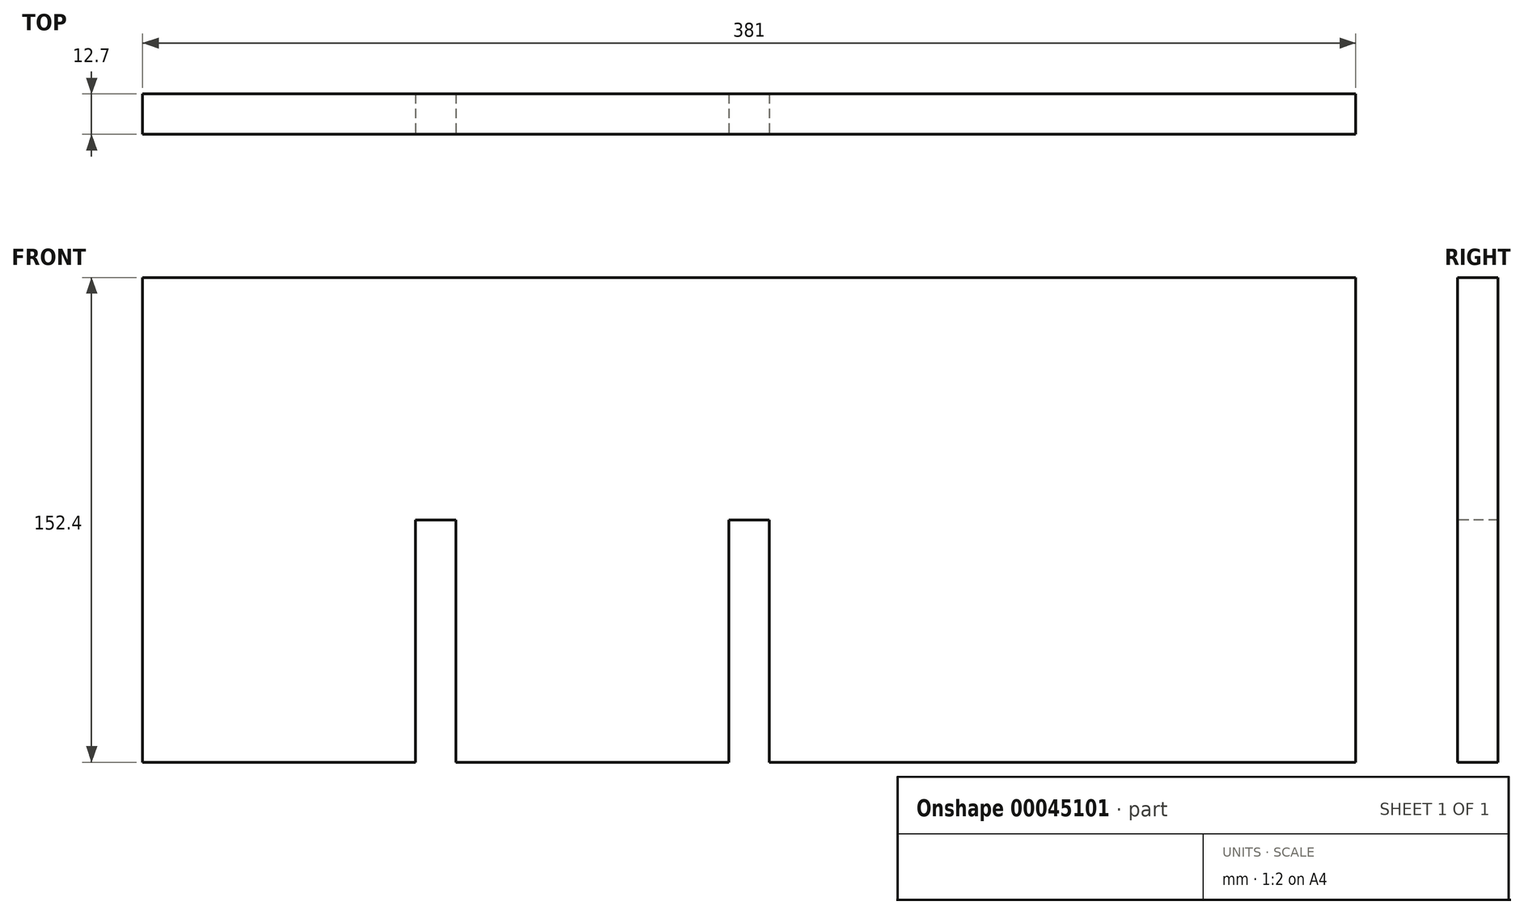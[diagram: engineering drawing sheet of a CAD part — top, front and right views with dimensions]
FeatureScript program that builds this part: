
annotation { "Feature Type Name" : "Feature", "Feature Type Description" : "" }
export const myFeature = defineFeature(function(context is Context, id is Id, definition is map)
    precondition{}
    {
        {
            var Q0;
            Q0=qCreatedBy(makeId("Front.planeOp"),FACE);
            var sketch = newSketch(context, id + "F0", { "sketchPlane" : qUnion([Q0])});
            skLineSegment(sketch, "E0.bottom", {"start": v(-134.6, 99.97) * mm, "end": v(246.4, 99.97) * mm});
            skLineSegment(sketch, "E0.top", {"start": v(-134.6, -52.43) * mm, "end": v(246.4, -52.43) * mm});
            skLineSegment(sketch, "E0.left", {"start": v(-134.6, 99.97) * mm, "end": v(-134.6, -52.43) * mm});
            skLineSegment(sketch, "E0.right", {"start": v(246.4, 99.97) * mm, "end": v(246.4, -52.43) * mm});
            skSolve(sketch);
        }
        {
            var Q0;
            Q0=makeQuery(id+"F0.imprint","IMPRINT",FACE,{"disambiguationData":[TD([[makeQuery(id+"F0.imprint","IMPRINT",EDGE,{"derivedFrom":sQuery(id+"F0.wireOp",EDGE,"E0.bottom")}),-1.0]])]});
            extrude(context, id + "F1", {"entities" : qUnion([Q0]), "depth" : 12.7 * mm});
        }
        {
            var Q0;
            Q0=makeQuery(id+"F1.opExtrude","CAP_FACE",FACE,{"disambiguationData":[OSD([sQuery(id+"F0.wireOp",EDGE,"E0.bottom"),sQuery(id+"F0.wireOp",EDGE,"E0.top"),sQuery(id+"F0.wireOp",EDGE,"E0.left"),sQuery(id+"F0.wireOp",EDGE,"E0.right")])],"isStart":false});
            var sketch = newSketch(context, id + "F2", { "sketchPlane" : qUnion([Q0])});
            skLineSegment(sketch, "E1.bottom", {"start": v(-48.87, -52.43) * mm, "end": v(-36.17, -52.43) * mm});
            skLineSegment(sketch, "E1.top", {"start": v(-48.87, 23.77) * mm, "end": v(-36.17, 23.77) * mm});
            skLineSegment(sketch, "E1.left", {"start": v(-48.87, -52.43) * mm, "end": v(-48.87, 23.77) * mm});
            skLineSegment(sketch, "E1.right", {"start": v(-36.17, -52.43) * mm, "end": v(-36.17, 23.77) * mm});
            skLineSegment(sketch, "E2.bottom", {"start": v(49.55, -52.43) * mm, "end": v(62.25, -52.43) * mm});
            skLineSegment(sketch, "E2.top", {"start": v(49.55, 23.77) * mm, "end": v(62.25, 23.77) * mm});
            skLineSegment(sketch, "E2.left", {"start": v(49.55, -52.43) * mm, "end": v(49.55, 23.77) * mm});
            skLineSegment(sketch, "E2.right", {"start": v(62.25, -52.43) * mm, "end": v(62.25, 23.77) * mm});
            skLineSegment(sketch, "E3.bottom", {"start": v(147.98, -52.43) * mm, "end": v(147.98, -52.43) * mm});
            skLineSegment(sketch, "E3.top", {"start": v(147.98, 23.77) * mm, "end": v(147.98, 23.77) * mm});
            skLineSegment(sketch, "E3.left", {"start": v(147.98, -52.43) * mm, "end": v(147.98, 23.77) * mm});
            skLineSegment(sketch, "E3.right", {"start": v(147.98, -52.43) * mm, "end": v(147.98, 23.77) * mm});
            skLineSegment(sketch, "E4.0", {"start": v(160.68, -52.43) * mm, "end": v(160.68, 23.77) * mm});
            skLineSegment(sketch, "E5", {"start": v(147.98, 23.77) * mm, "end": v(160.68, 23.77) * mm});
            skSolve(sketch);
        }
        {
            var Q0;
            Q0=makeQuery(id+"F2.imprint","IMPRINT",FACE,{"disambiguationData":[TD([[makeQuery(id+"F2.imprint","IMPRINT",EDGE,{"derivedFrom":sQuery(id+"F2.wireOp",EDGE,"E1.bottom")}),1.0]])]});
            var Q1;
            Q1=makeQuery(id+"F2.imprint","IMPRINT",FACE,{"disambiguationData":[TD([[makeQuery(id+"F2.imprint","IMPRINT",EDGE,{"derivedFrom":sQuery(id+"F2.wireOp",EDGE,"E2.bottom")}),1.0]])]});
            var Q2;
            {var subQ2=sQuery(id+"F2.wireOp",EDGE,"E3.right");Q2=makeQuery(id+"F2.imprint","IMPRINT",FACE,{"disambiguationData":[TD([[makeQuery(id+"F2.imprint","IMPRINT",EDGE,{"derivedFrom":subQ2}),-1.0]])]});}
            extrude(context, id + "F3", {"entities" : qUnion([Q0, Q1, Q2]), "operationType" : NewBodyOperationType.REMOVE, "oppositeDirection" : true, "depth" : 12.7 * mm});
        }
    });
